# Revit family: Differenzdruckregler 4002 5-30kPa
name_source: partatom
category: Rohrzubehör
revit_build: Autodesk Revit 2018 (Build: 20190510_1515(x64)
units: mm (PartAtom-declared; Revit-internal decimal feet)

## family parameters
Arbeitsebenenbasiert = Nein
Beim Laden mit Abzugskörper schneiden = Nein
Bemaßung runder Anschluss = Durchmesser verwenden
Gemeinsam genutzt = Nein
Immer vertikal = Ja
OmniClass-Nummer = 23.65.55.14
OmniClass-Titel = Valves for Liquid Services
Teiletyp = Unterbricht

## types (2) — shared parameters
Anschlussnippel = Messing CW602N
Anwendungsgebiet = Der Differenzdruckregler ist ein Regler mit linearer Kennlinie in Geradsitzausführung und arbeitet ohne
Hilfsenergie. Der gewünschte Differenzdruck-Sollwert kann zwischen 5 und 30 kPa; 25 und 60 kPa bzw.
45 und 80 kPa stufenlos eingestellt werden. Der eingestellte Wert ist mit Hilfe des Einstelldiagrammes
ablesbar. Werksseitig ist der Sollwert auf Minimum eingestellt. Der erforderliche Sollwert wird mit dem
Einstellwerkzeug (1 4006 02) eingestellt. Im Lieferumfang enthalten ist die Impulsleitung (1000 mm),
diese ist im Vorlauf einzubinden.
Anzeigehülse = Kunststoff (Rot)
B01 = 10 mm  [stored 0.0328084 ft]
B02 = 104.688 mm  [stored 0.343465 ft]
B03 = 44.5 mm  [stored 0.145997 ft]
B04 = 100.649 mm  [stored 0.330213 ft]
Druckfeder = Federstahl 14310 NS
Dämmschale = EPP (expandiertes Polypropylen)
Einstellspindel = Messing CW614N
Gehäuse = DZR Messing CC770S
H03 = 9.8 mm  [stored 0.0321522 ft]
H04 = 4 mm  [stored 0.0131234 ft]
Hersteller = HERZ-Armaturen Ges.m.b.H
Hinweise zum Material = Gemäß Art 33 der REACH-Verordnung (EG Nr. 1907/2006) sind wir verpflichtet, darauf hinzuweisen,
dass der Stoff Blei auf der SVHC-Liste geführt wird und dass alle aus Messing bestehenden Bauteile,
die in unseren Erzeugnissen verarbeitet sind, mehr als 0,1 % (w/w) Blei (CAS: 7439-92-1 / EINECS:
231-100-4) enthalten. Da Blei als Legierungsbestandteil fest gebunden ist, sind keine Expositionen zu
erwarten und daher sind keine zusätzlichen Angaben zur sicheren Verwendung notwendig.

Im Hanf enthaltenes Ammoniak schädigt
Messingventilgehäuse, EPDM Dichtungen werden durch
Mineralöle bzw. mineralölhaltige Schmierstoffe aufgequollen
und führen somit zum Ausfall der EPDM-Dichtungen. Für
Frost- und Korrosionsschutzmittel auf der Basis von Ethylen- und Propylenglykol sind die entsprechenden
Angaben den Unterlagen des Herstellers zu entnehmen.
J1 = 6.5 mm
J10 = 18.897 mm  [stored 0.061998 ft]
J11 = 3.5 mm  [stored 0.0114829 ft]
J2 = 11 mm  [stored 0.0360892 ft]
J3 = 3.2 mm  [stored 0.0104987 ft]
J4 = 1.5 mm  [stored 0.00492126 ft]
J5 = 6.5 mm
J6 = 3.9 mm  [stored 0.0127953 ft]
J7 = 15.897 mm
J8 = 7.85 mm  [stored 0.0257546 ft]
J9 = 15.7 mm  [stored 0.0515092 ft]
K1 = 6.651 mm  [stored 0.0218209 ft]
K1.1 = 2.35 mm  [stored 0.00770997 ft]
K10 = 18.25 mm  [stored 0.0598753 ft]
K11 = 35 mm  [stored 0.114829 ft]
K12 = 10 mm  [stored 0.0328084 ft]
K13 = 16.649 mm  [stored 0.0546227 ft]
K14 = 16.649 mm  [stored 0.0546227 ft]
K15 = 26.649 mm  [stored 0.0874311 ft]
K16 = 3 mm  [stored 0.00984252 ft]
K17 = 66.7 mm  [stored 0.218832 ft]
K18 = 89 mm  [stored 0.291995 ft]
K2 = 2.35 mm  [stored 0.00770997 ft]
K3 = 15 mm  [stored 0.0492126 ft]
K4 = 12 mm  [stored 0.0393701 ft]
K5 = 13 mm
K6 = 11.7 mm  [stored 0.0383858 ft]
K7 = 8.7 mm  [stored 0.0285433 ft]
K8 = 55 mm  [stored 0.180446 ft]
K9 = 4 mm  [stored 0.0131234 ft]
Max. Betriebsdruck = 1600000.0 Pa
Max. Differenzdruck am Gehäuse = 400000.0 Pa
Max. zulässige Betriebstemperatur DN40 - DN50 = 110 °C
Max. zulässige Betriebstemperatur bis DN32 = 130 °C
Medium = Wasserbeschaffenheit nach ÖNORM H 5195 und VDI 2035
Die Verwendung von Ethylen- und Propylenglykol ist im
Mischungsverhältnis 25 - 50 Vol.-% zulässig.
Membrane = EPDM
Membrangehäuse = Messing CW602N
Min. Betriebstemperatur (Frostschutz) = -20 °C
Min. Betriebstemperatur (reines Wasser) = 2 °C
O-Ringe = EPDM
PN = 16
R02 = 14.5 mm  [stored 0.0475722 ft]
Regelbereich = 5 - 30kPa
Regleranschlussmutter = Messing CW614N
S07 = 10 mm  [stored 0.0328084 ft]
SCRNCODE = 05;03;4
SCRNSEQ = ARM;ARM_TYP="DIFR";2
URL = www.herz-armaturen.at
V10 = 16 mm  [stored 0.0524934 ft]
V12 = 17 mm
VRL01 = 30 mm  [stored 0.0984252 ft]
Ventilschaft = Edelstahl 14301

## per-type parameters (varying)
| type | Dämmung |
| Mit Dämmung | Ja |
| Ohne Dämmung | Nein |

note: [stored X ft] marks values corroborated as IEEE doubles in the binary element streams (Revit-internal decimal feet)
